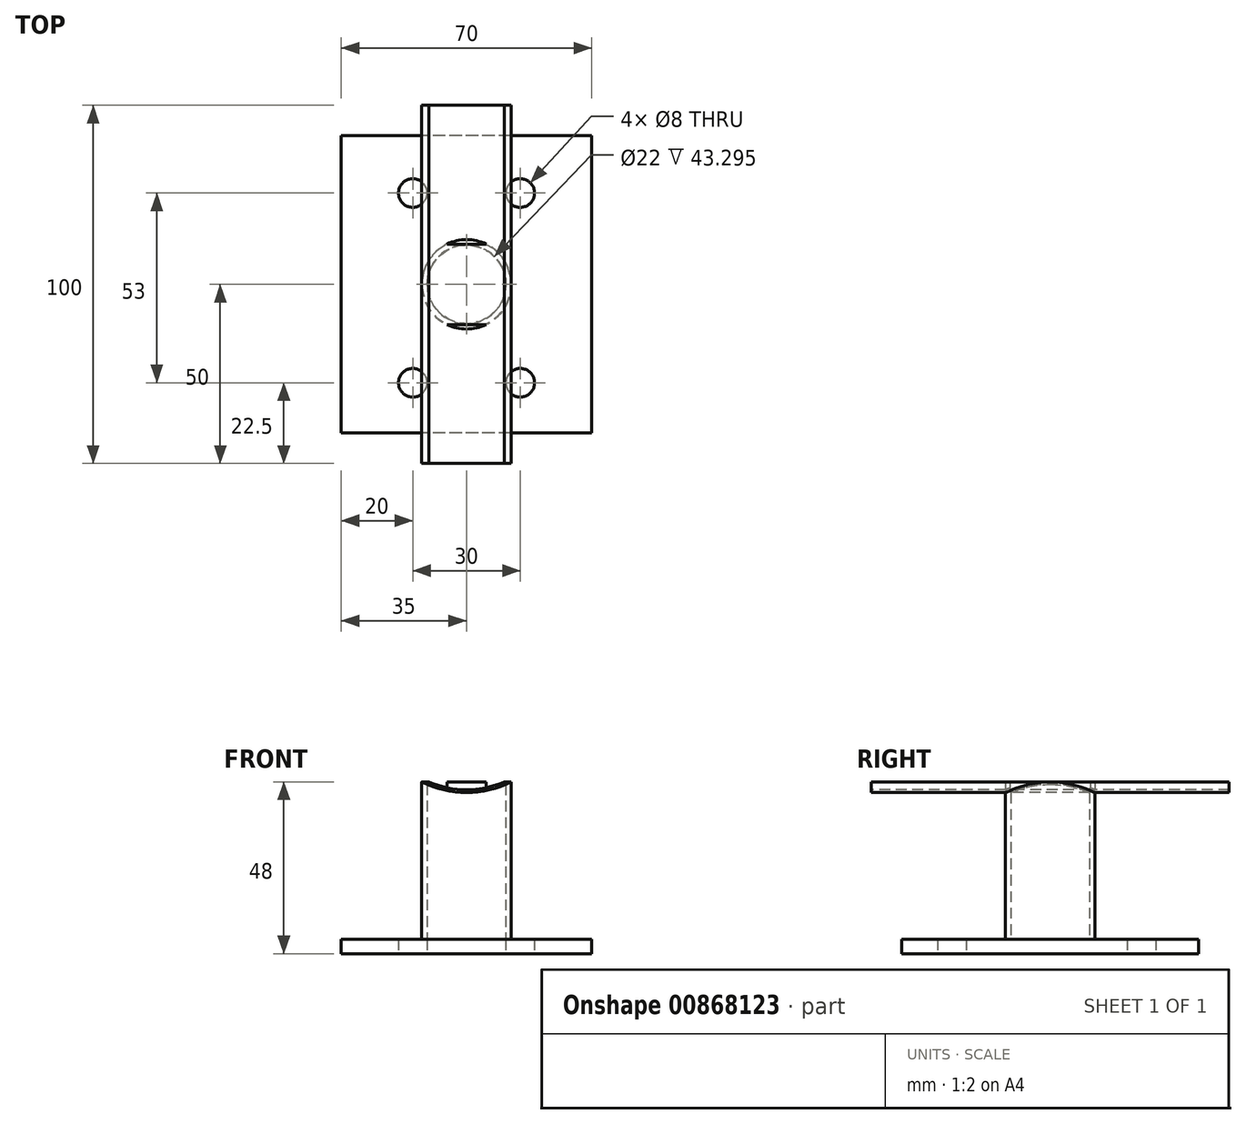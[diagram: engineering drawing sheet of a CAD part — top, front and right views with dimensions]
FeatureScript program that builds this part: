
annotation { "Feature Type Name" : "Feature", "Feature Type Description" : "" }
export const myFeature = defineFeature(function(context is Context, id is Id, definition is map)
    precondition{}
    {
        {
            var Q0;
            Q0=qCreatedBy(makeId("Top.planeOp"),FACE);
            var sketch = newSketch(context, id + "F0", { "sketchPlane" : qUnion([Q0])});
            skLineSegment(sketch, "E0.bottom", {"start": v(35, 41.5) * mm, "end": v(-35, 41.5) * mm});
            skLineSegment(sketch, "E0.top", {"start": v(35, -41.5) * mm, "end": v(-35, -41.5) * mm});
            skLineSegment(sketch, "E0.left", {"start": v(35, 41.5) * mm, "end": v(35, -41.5) * mm});
            skLineSegment(sketch, "E0.right", {"start": v(-35, 41.5) * mm, "end": v(-35, -41.5) * mm});
            skPoint(sketch, "E0.middle", {"position": v(0, 0) * mm});
            skSolve(sketch);
        }
        {
            var Q0;
            Q0=makeQuery(id+"F0.imprint","IMPRINT",FACE,{"disambiguationData":[TD([[makeQuery(id+"F0.imprint","IMPRINT",EDGE,{"derivedFrom":sQuery(id+"F0.wireOp",EDGE,"E0.bottom")}),1.0]])]});
            extrude(context, id + "F1", {"entities" : qUnion([Q0]), "oppositeDirection" : true, "depth" : 4 * mm, "offsetDistance" : 25 * mm});
        }
        {
            var Q0;
            Q0=makeQuery(id+"F1.opExtrude","CAP_FACE",FACE,{"disambiguationData":[OSD([sQuery(id+"F0.wireOp",EDGE,"E0.bottom"),sQuery(id+"F0.wireOp",EDGE,"E0.top"),sQuery(id+"F0.wireOp",EDGE,"E0.left"),sQuery(id+"F0.wireOp",EDGE,"E0.right")])],"isStart":true});
            var sketch = newSketch(context, id + "F2", { "sketchPlane" : qUnion([Q0])});
            skCircle(sketch, "E1", {"center": v(0, 0) * mm, "radius": 12.5 * mm});
            skCircle(sketch, "E2.0", {"center": v(0, 0) * mm, "radius": 11 * mm});
            skSolve(sketch);
        }
        {
            var Q0;
            Q0=makeQuery(id+"F2.imprint","IMPRINT",FACE,{"disambiguationData":[TD([[makeQuery(id+"F2.imprint","IMPRINT",EDGE,{"derivedFrom":sQuery(id+"F2.wireOp",EDGE,"E1")}),1.0]])]});
            extrude(context, id + "F3", {"entities" : qUnion([Q0]), "operationType" : NewBodyOperationType.ADD, "depth" : 44 * mm, "offsetDistance" : 25 * mm});
        }
        {
            var Q0;
            Q0=qCreatedBy(makeId("Front.planeOp"),FACE);
            var sketch = newSketch(context, id + "F4", { "sketchPlane" : qUnion([Q0])});
            skLineSegment(sketch, "E3", {"start": v(0, 0) * mm, "end": v(0, 44) * mm, "construction": true});
            skArc(sketch, "E4", {"start": v(-12.5, 44) * mm, "mid": v(0, 41) * mm, "end": v(12.5, 44) * mm});
            skLineSegment(sketch, "E5", {"start": v(-12.5, 44) * mm, "end": v(-10.5, 44) * mm});
            skLineSegment(sketch, "E6", {"start": v(-10.5, 44) * mm, "end": v(10.5, 44) * mm});
            skLineSegment(sketch, "E7", {"start": v(10.5, 44) * mm, "end": v(12.5, 44) * mm});
            skArc(sketch, "E8", {"start": v(-10.5, 44) * mm, "mid": v(0, 41.74) * mm, "end": v(10.5, 44) * mm});
            skSolve(sketch);
        }
        {
            var Q0;
            Q0=makeQuery(id+"F4.imprint","IMPRINT",FACE,{"disambiguationData":[TD([[makeQuery(id+"F4.imprint","IMPRINT",EDGE,{"derivedFrom":sQuery(id+"F4.wireOp",EDGE,"E6")}),-1.0]])]});
            var Q1;
            Q1=makeQuery(id+"F4.imprint","IMPRINT",FACE,{"disambiguationData":[TD([[makeQuery(id+"F4.imprint","IMPRINT",EDGE,{"derivedFrom":sQuery(id+"F4.wireOp",EDGE,"E4")}),1.0]])]});
            extrude(context, id + "F5", {"entities" : qUnion([Q0, Q1]), "operationType" : NewBodyOperationType.REMOVE, "endBound" : BoundingType.SYMMETRIC, "depth" : 22.5 * mm, "offsetDistance" : 25 * mm});
        }
        {
            var Q0;
            Q0=makeQuery(id+"F1.opExtrude","CAP_FACE",FACE,{"disambiguationData":[OSD([sQuery(id+"F0.wireOp",EDGE,"E0.bottom"),sQuery(id+"F0.wireOp",EDGE,"E0.top"),sQuery(id+"F0.wireOp",EDGE,"E0.left"),sQuery(id+"F0.wireOp",EDGE,"E0.right")])],"isStart":false});
            var sketch = newSketch(context, id + "F6", { "sketchPlane" : qUnion([Q0])});
            skLineSegment(sketch, "E9", {"start": v(-35, 41.5) * mm, "end": v(35, -41.5) * mm, "construction": true});
            skLineSegment(sketch, "E10", {"start": v(35, -41.5) * mm, "end": v(35, 41.5) * mm, "construction": true});
            skLineSegment(sketch, "E11", {"start": v(35, 41.5) * mm, "end": v(-35, -41.5) * mm, "construction": true});
            skLineSegment(sketch, "E12", {"start": v(-35, -41.5) * mm, "end": v(-35, 41.5) * mm, "construction": true});
            skLineSegment(sketch, "E13", {"start": v(-35, -41.5) * mm, "end": v(35, -41.5) * mm, "construction": true});
            skCircle(sketch, "E14", {"center": v(-15, 27.5) * mm, "radius": 4 * mm});
            skCircle(sketch, "E15.0.1.0", {"center": v(-15, -25.5) * mm, "radius": 4 * mm});
            skCircle(sketch, "E15.1.0.0", {"center": v(15, 27.5) * mm, "radius": 4 * mm});
            skCircle(sketch, "E15.1.1.0", {"center": v(15, -25.5) * mm, "radius": 4 * mm});
            skLineSegment(sketch, "E15.direction1", {"start": v(-15, 27.5) * mm, "end": v(15, 27.5) * mm, "construction": true});
            skLineSegment(sketch, "E15.direction2", {"start": v(-15, 27.5) * mm, "end": v(-15, -25.5) * mm, "construction": true});
            skSolve(sketch);
        }
        {
            var Q0;
            Q0=makeQuery(id+"F6.imprint","IMPRINT",FACE,{"disambiguationData":[TD([[makeQuery(id+"F6.imprint","IMPRINT",EDGE,{"derivedFrom":sQuery(id+"F6.wireOp",EDGE,"E14")}),1.0]])]});
            var Q1;
            Q1=makeQuery(id+"F6.imprint","IMPRINT",FACE,{"disambiguationData":[TD([[makeQuery(id+"F6.imprint","IMPRINT",EDGE,{"derivedFrom":sQuery(id+"F6.wireOp",EDGE,"E15.1.0.0")}),1.0]])]});
            var Q2;
            Q2=makeQuery(id+"F6.imprint","IMPRINT",FACE,{"disambiguationData":[TD([[makeQuery(id+"F6.imprint","IMPRINT",EDGE,{"derivedFrom":sQuery(id+"F6.wireOp",EDGE,"E15.1.1.0")}),1.0]])]});
            var Q3;
            Q3=makeQuery(id+"F6.imprint","IMPRINT",FACE,{"disambiguationData":[TD([[makeQuery(id+"F6.imprint","IMPRINT",EDGE,{"derivedFrom":sQuery(id+"F6.wireOp",EDGE,"E15.0.1.0")}),1.0]])]});
            extrude(context, id + "F7", {"entities" : qUnion([Q0, Q1, Q2, Q3]), "operationType" : NewBodyOperationType.REMOVE, "oppositeDirection" : true, "depth" : 25 * mm, "offsetDistance" : 25 * mm});
        }
        {
            var Q0;
            Q0=qCreatedBy(makeId("Right.planeOp"),FACE);
            var sketch = newSketch(context, id + "F8", { "sketchPlane" : qUnion([Q0])});
            skLineSegment(sketch, "E16", {"start": v(50, 37) * mm, "end": v(-50, 37) * mm});
            skSolve(sketch);
        }
        {
            var Q0;
            Q0=makeQuery(id+"F4.imprint","IMPRINT",FACE,{"disambiguationData":[TD([[makeQuery(id+"F4.imprint","IMPRINT",EDGE,{"derivedFrom":sQuery(id+"F4.wireOp",EDGE,"E4")}),1.0]])]});
            var Q1;
            Q1 = qConstructionFilter(qBodyType(qCreatedBy(id + "F8" ,EDGE), BodyType.WIRE), ConstructionObject.NO);
            sweep(context, id + "F9", {"operationType" : NewBodyOperationType.ADD, "profiles" : qUnion([Q0]), "path" : qUnion([Q1])});
        }
    });
